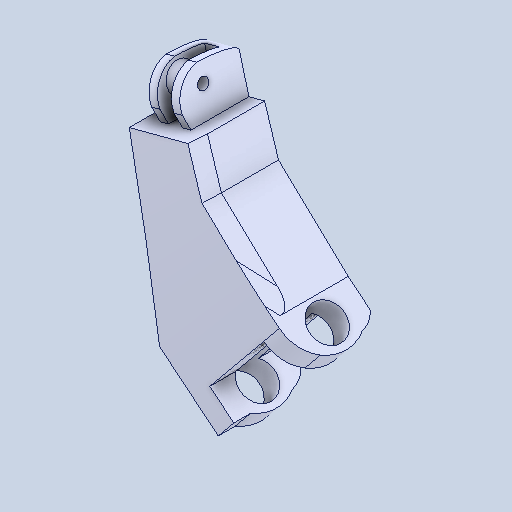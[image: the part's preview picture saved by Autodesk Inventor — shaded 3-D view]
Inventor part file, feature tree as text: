
AUTODESK INVENTOR PART (.ipt)
format: ipt  version: 2022 (Build 260153000, 153)  size: 161,280 bytes
history: mixed  units: mm
features: other x1, fillet x1, imported_body x1
ambient origin geometry x8: Origin, YZ Plane, XZ Plane, XY Plane, X Axis, Y Axis, Z Axis, Center Point
bodies: Body1 (imported_parasolid)
feature tree (3):
  other  "Sólido1"
  fillet  "Fillet4"  [1 undecoded]
  imported_body  NMx_Import_Brep_tag  [imported B-rep: ~6 faces, bbox_mm=None]
note: 1 required parameter value undecoded (feature->parameter linkage not recoverable at this tier; creation-order binding heuristic only, values carry confidence <= 0.55)
